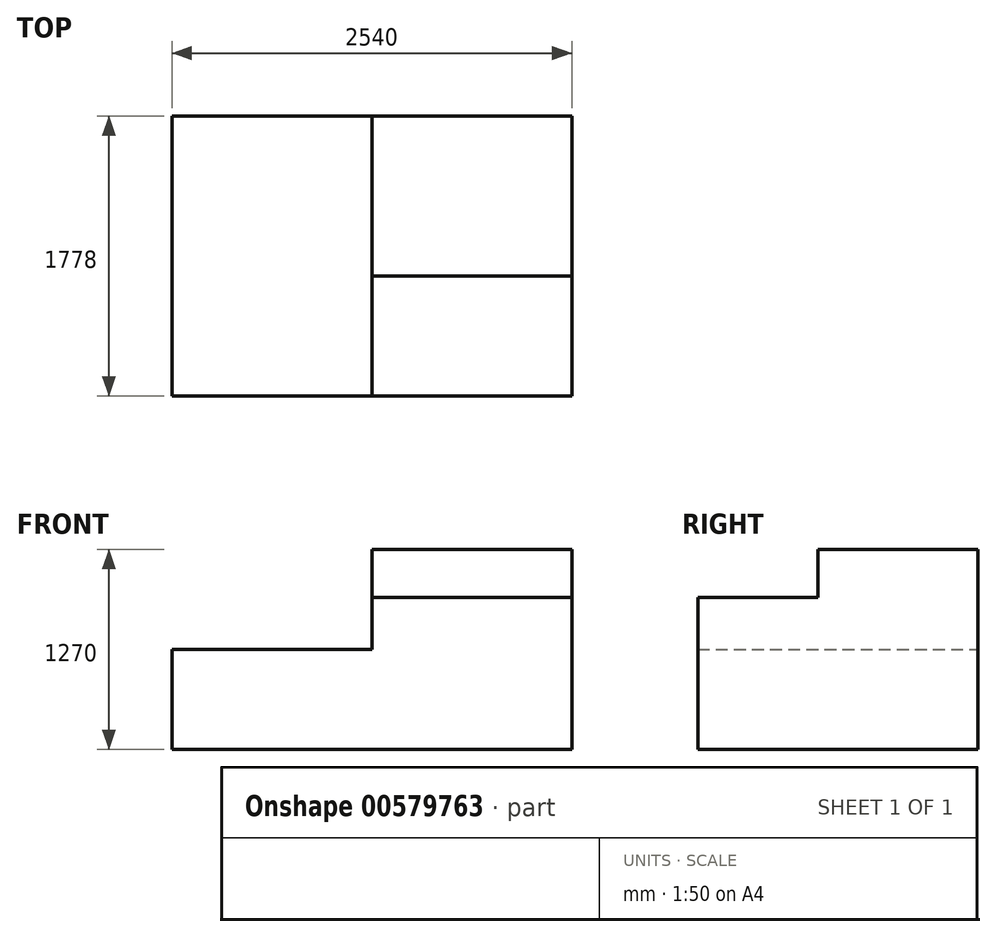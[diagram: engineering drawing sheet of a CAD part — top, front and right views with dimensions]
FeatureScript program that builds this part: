
annotation { "Feature Type Name" : "Feature", "Feature Type Description" : "" }
export const myFeature = defineFeature(function(context is Context, id is Id, definition is map)
    precondition{}
    {
        {
            var Q0;
            Q0=qCreatedBy(makeId("Top.planeOp"),FACE);
            var sketch = newSketch(context, id + "F0", { "sketchPlane" : qUnion([Q0])});
            skLineSegment(sketch, "E0.bottom", {"start": v(0, 0) * mm, "end": v(1270, 0) * mm});
            skLineSegment(sketch, "E0.top", {"start": v(0, 1778) * mm, "end": v(1270, 1778) * mm});
            skLineSegment(sketch, "E0.left", {"start": v(0, 0) * mm, "end": v(0, 1778) * mm});
            skLineSegment(sketch, "E0.right", {"start": v(1270, 0) * mm, "end": v(1270, 1778) * mm});
            skLineSegment(sketch, "E1.bottom", {"start": v(1270, 1778) * mm, "end": v(2540, 1778) * mm});
            skLineSegment(sketch, "E1.top", {"start": v(1270, 762) * mm, "end": v(2540, 762) * mm});
            skLineSegment(sketch, "E1.left", {"start": v(1270, 1778) * mm, "end": v(1270, 762) * mm});
            skLineSegment(sketch, "E1.right", {"start": v(2540, 1778) * mm, "end": v(2540, 762) * mm});
            skLineSegment(sketch, "E2.top", {"start": v(1270, 0) * mm, "end": v(2540, 0) * mm});
            skLineSegment(sketch, "E2.left", {"start": v(1270, 762) * mm, "end": v(1270, 0) * mm});
            skLineSegment(sketch, "E2.right", {"start": v(2540, 762) * mm, "end": v(2540, 0) * mm});
            skSolve(sketch);
        }
        {
            var Q0;
            Q0=makeQuery(id+"F0.imprint","IMPRINT",FACE,{"disambiguationData":[TD([[makeQuery(id+"F0.imprint","IMPRINT",EDGE,{"derivedFrom":sQuery(id+"F0.wireOp",EDGE,"E0.bottom")}),1.0]])]});
            var sketch = newSketch(context, id + "F1", { "sketchPlane" : qUnion([Q0])});
            skSolve(sketch);
        }
        {
            var Q0;
            Q0 = qSketchRegion(id + "F1", true);
            var Q1;
            Q1=makeQuery(id+"F0.imprint","IMPRINT",FACE,{"disambiguationData":[TD([[makeQuery(id+"F0.imprint","IMPRINT",EDGE,{"derivedFrom":sQuery(id+"F0.wireOp",EDGE,"E0.bottom")}),1.0]])]});
            extrude(context, id + "F2", {"entities" : qUnion([Q0, Q1]), "depth" : 635 * mm, "offsetDistance" : 25.4 * mm});
        }
        {
            var Q0;
            Q0=makeQuery(id+"F0.imprint","IMPRINT",FACE,{"disambiguationData":[TD([[makeQuery(id+"F0.imprint","IMPRINT",EDGE,{"derivedFrom":sQuery(id+"F0.wireOp",EDGE,"E1.bottom")}),-1.0]])]});
            extrude(context, id + "F3", {"entities" : qUnion([Q0]), "operationType" : NewBodyOperationType.ADD, "depth" : 1270 * mm, "offsetDistance" : 25.4 * mm});
        }
        {
            var Q0;
            Q0=makeQuery(id+"F0.imprint","IMPRINT",FACE,{"disambiguationData":[TD([[makeQuery(id+"F0.imprint","IMPRINT",EDGE,{"derivedFrom":sQuery(id+"F0.wireOp",EDGE,"E1.top")}),-1.0]])]});
            extrude(context, id + "F4", {"entities" : qUnion([Q0]), "operationType" : NewBodyOperationType.ADD, "depth" : 965.2 * mm, "offsetDistance" : 25.4 * mm});
        }
    });
